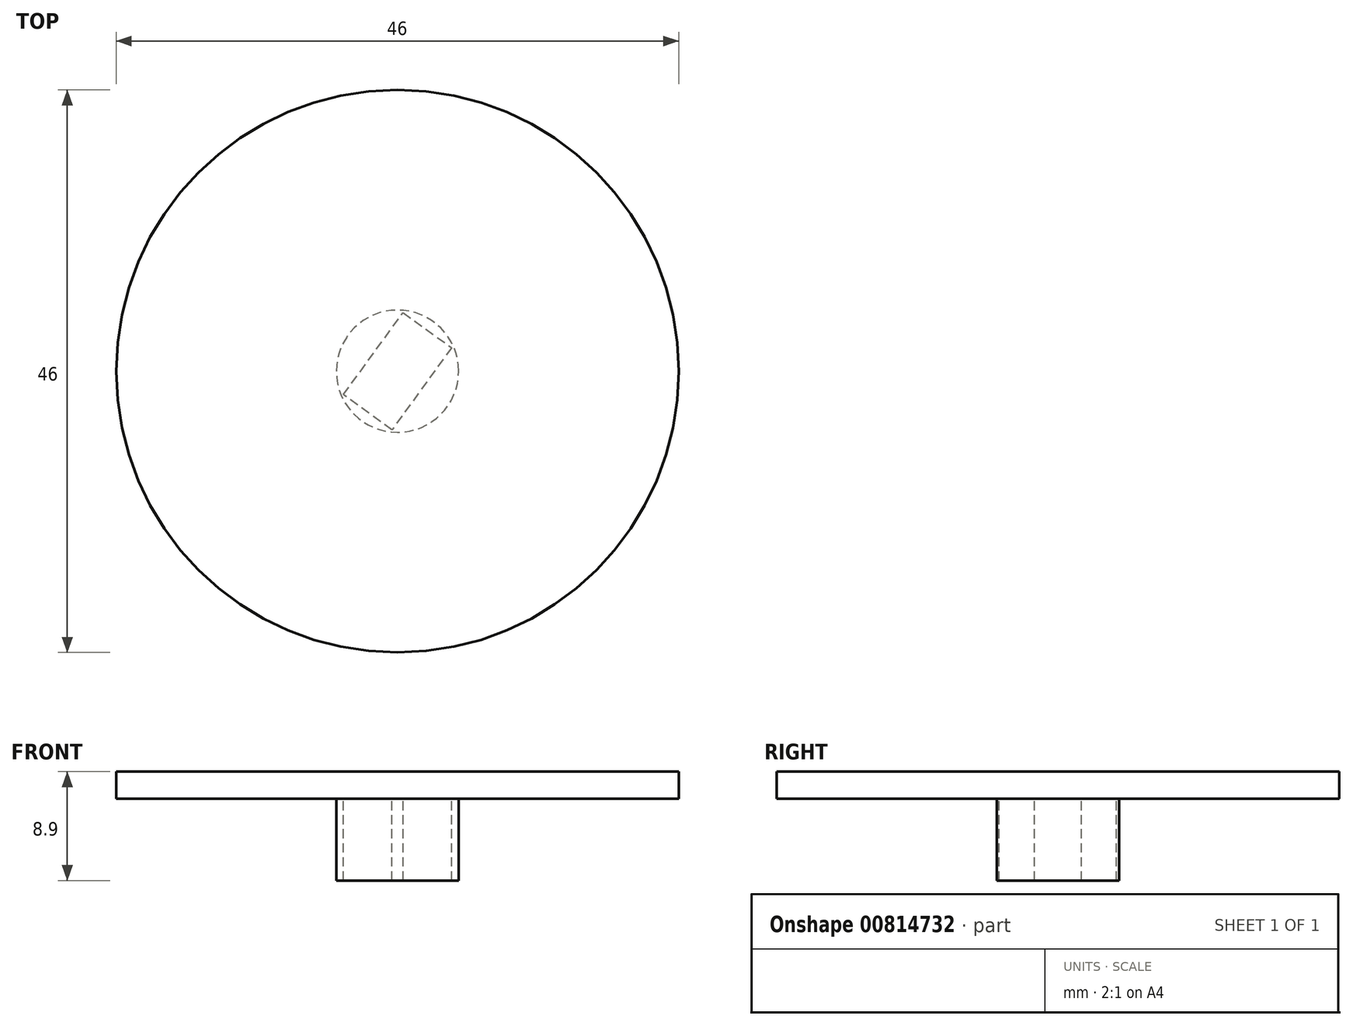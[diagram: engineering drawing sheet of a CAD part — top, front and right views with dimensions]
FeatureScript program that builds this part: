
annotation { "Feature Type Name" : "Feature", "Feature Type Description" : "" }
export const myFeature = defineFeature(function(context is Context, id is Id, definition is map)
    precondition{}
    {
        {
            var Q0;
            Q0=qCreatedBy(makeId("Front.planeOp"),FACE);
            var sketch = newSketch(context, id + "F0", { "sketchPlane" : qUnion([Q0])});
            skLineSegment(sketch, "E0", {"start": v(0, 0) * mm, "end": v(5, 0) * mm});
            skLineSegment(sketch, "E1", {"start": v(5, 0) * mm, "end": v(5, 6.7) * mm});
            skLineSegment(sketch, "E2", {"start": v(5, 6.7) * mm, "end": v(23, 6.7) * mm});
            skLineSegment(sketch, "E3", {"start": v(23, 6.7) * mm, "end": v(23, 8.9) * mm});
            skLineSegment(sketch, "E4", {"start": v(23, 8.9) * mm, "end": v(0, 8.9) * mm});
            skLineSegment(sketch, "E5", {"start": v(0, 8.9) * mm, "end": v(0, 0) * mm});
            skSolve(sketch);
        }
        {
            var Q0;
            Q0=makeQuery(id+"F0.imprint","IMPRINT",FACE,{"disambiguationData":[TD([[makeQuery(id+"F0.imprint","IMPRINT",EDGE,{"derivedFrom":sQuery(id+"F0.wireOp",EDGE,"E0")}),1.0]])]});
            var Q1;
            Q1=sQuery(id+"F0.wireOp",EDGE,"E5");
            revolve(context, id + "F1", {"surfaceOperationType" : NewSurfaceOperationType.NEW, "entities" : qUnion([Q0]), "axis" : qUnion([Q1]), "revolveType" : RevolveType.FULL});
        }
        {
            var Q0;
            Q0=makeQuery(id+"F1.opRevolve","SWEPT_FACE",FACE,{"disambiguationData":[OSD([sQuery(id+"F0.wireOp",EDGE,"E2")])]});
            var sketch = newSketch(context, id + "F2", { "sketchPlane" : qUnion([Q0])});
            skLineSegment(sketch, "E6", {"start": v(0.46, -4.8) * mm, "end": v(-4.42, 1.92) * mm});
            skLineSegment(sketch, "E7", {"start": v(-4.42, 1.92) * mm, "end": v(-0.46, 4.8) * mm});
            skLineSegment(sketch, "E8", {"start": v(-0.46, 4.8) * mm, "end": v(4.42, -1.92) * mm});
            skLineSegment(sketch, "E9", {"start": v(4.42, -1.92) * mm, "end": v(0.46, -4.8) * mm});
            skLineSegment(sketch, "E10", {"start": v(-7.98, 2.6) * mm, "end": v(9.14, -2.97) * mm, "construction": true});
            skLineSegment(sketch, "E11", {"start": v(-4.42, 1.92) * mm, "end": v(4.42, -1.92) * mm, "construction": true});
            skSolve(sketch);
        }
        {
            var Q0;
            Q0 = qSketchRegion(id + "F2", true);
            var Q1;
            Q1=makeQuery(id+"F1.opRevolve","SWEPT_FACE",FACE,{"disambiguationData":[OSD([sQuery(id+"F0.wireOp",EDGE,"E0")])]});
            extrude(context, id + "F3", {"entities" : qUnion([Q0]), "operationType" : NewBodyOperationType.REMOVE, "endBound" : BoundingType.UP_TO_SURFACE, "depth" : 16.8 * mm, "endBoundEntityFace" : qUnion([Q1]), "offsetDistance" : 25 * mm});
        }
    });
